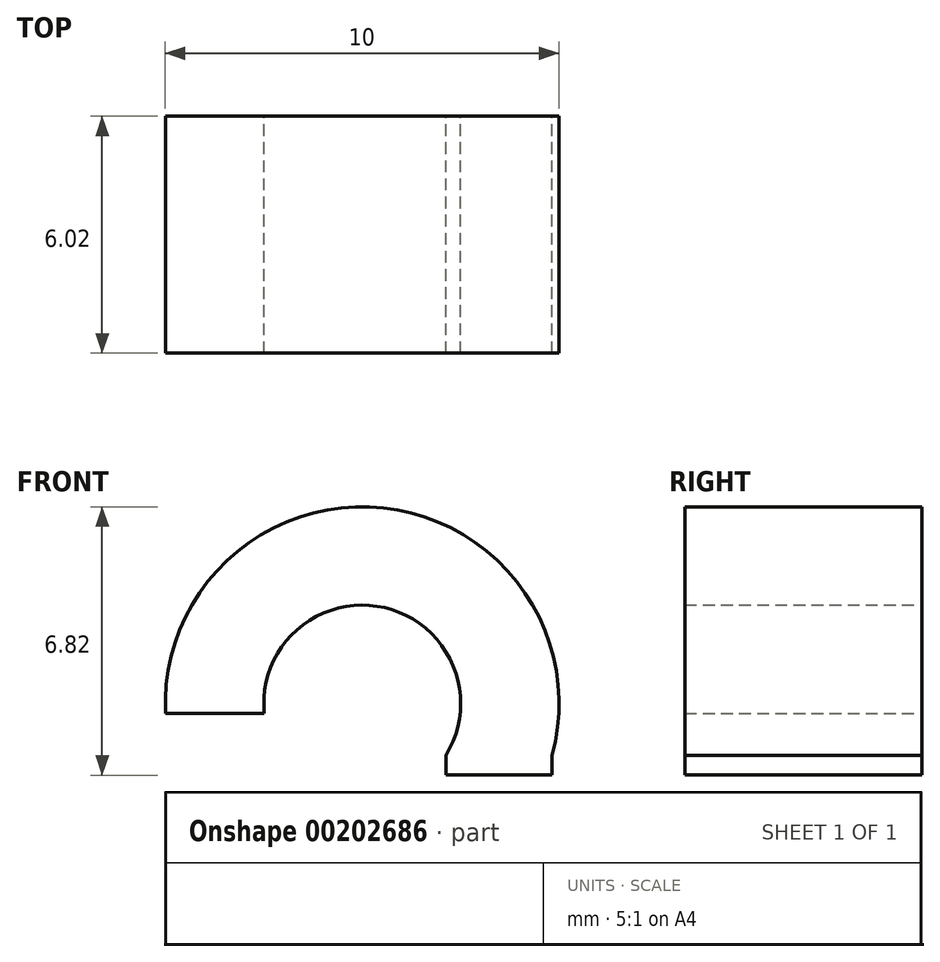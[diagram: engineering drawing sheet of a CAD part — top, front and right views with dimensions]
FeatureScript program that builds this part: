
annotation { "Feature Type Name" : "Feature", "Feature Type Description" : "" }
export const myFeature = defineFeature(function(context is Context, id is Id, definition is map)
    precondition{}
    {
        {
            var Q0;
            Q0=qCreatedBy(makeId("Front.planeOp"),FACE);
            var sketch = newSketch(context, id + "F0", { "sketchPlane" : qUnion([Q0])});
            skArc(sketch, "E0", {"start": v(-16.16, 1.21) * mm, "mid": v(-20.45, 7.5) * mm, "end": v(-25.98, 2.28) * mm});
            skArc(sketch, "E1", {"start": v(-18.86, 1.21) * mm, "mid": v(-20.42, 4.97) * mm, "end": v(-23.47, 2.28) * mm});
            skLineSegment(sketch, "E2.trimOffspring", {"start": v(-18.86, 1.21) * mm, "end": v(-16.16, 1.21) * mm});
            skLineSegment(sketch, "E3", {"start": v(-25.98, 2.28) * mm, "end": v(-23.47, 2.28) * mm});
            skSolve(sketch);
        }
        {
            var Q0;
            Q0 = qSketchRegion(id + "F0", true);
            extrude(context, id + "F1", {"entities" : qUnion([Q0]), "depth" : 6.02 * mm});
        }
        {
            var Q0;
            Q0=makeQuery(id+"F1.opExtrude","SWEPT_FACE",FACE,{"disambiguationData":[OSD([sQuery(id+"F0.wireOp",EDGE,"E2.trimOffspring")])]});
            extrude(context, id + "F2", {"entities" : qUnion([Q0]), "operationType" : NewBodyOperationType.ADD, "depth" : .5 * mm});
        }
    });
